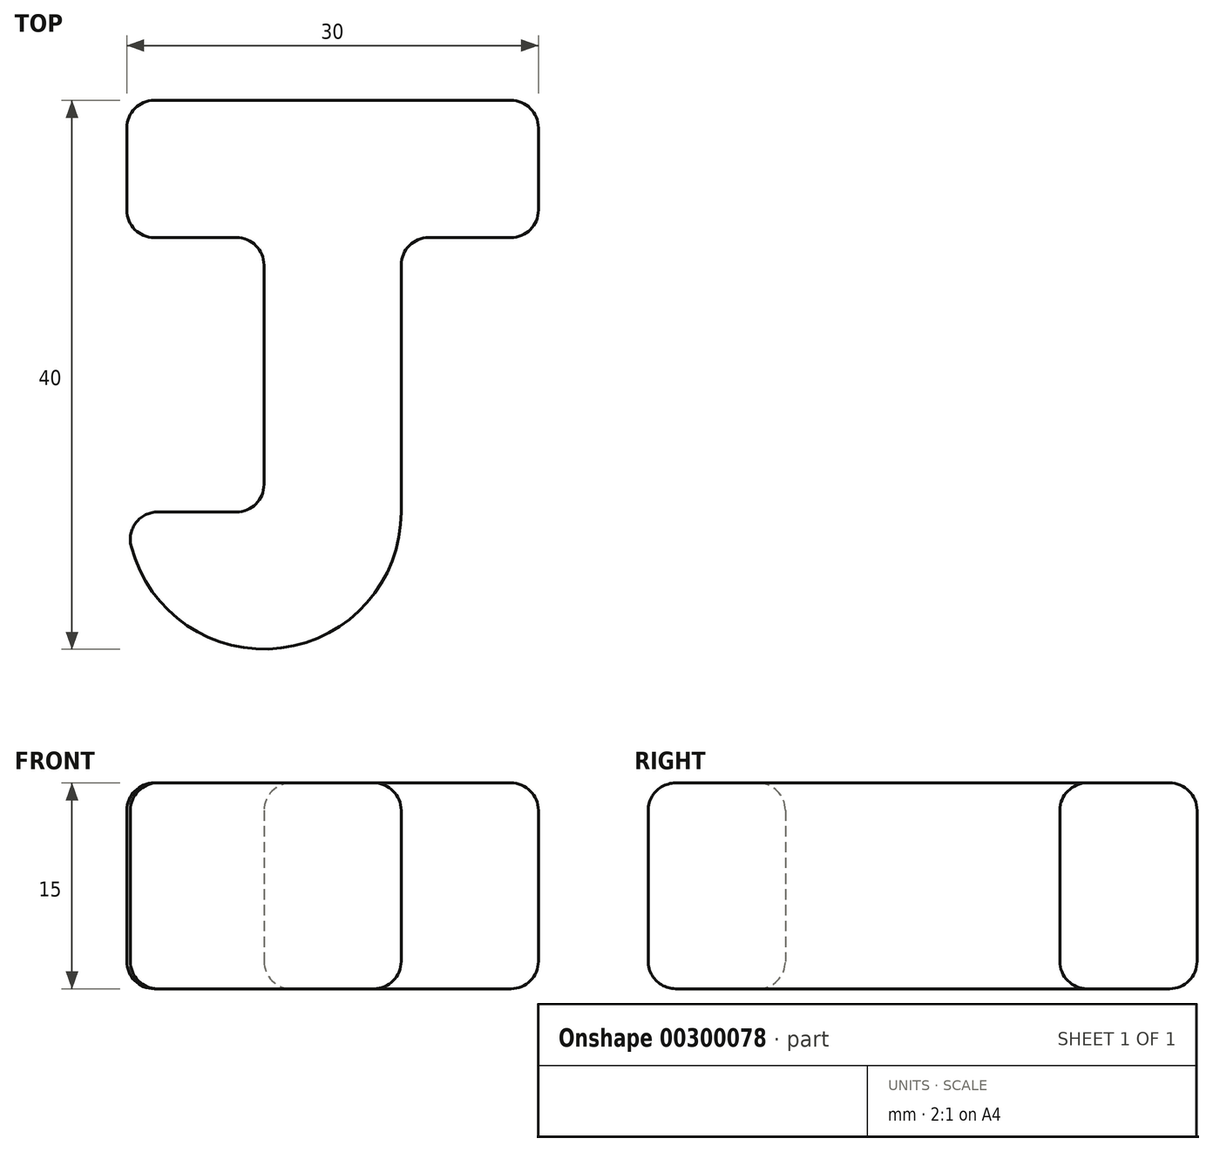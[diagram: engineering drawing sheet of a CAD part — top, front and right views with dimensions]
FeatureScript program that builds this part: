
annotation { "Feature Type Name" : "Feature", "Feature Type Description" : "" }
export const myFeature = defineFeature(function(context is Context, id is Id, definition is map)
    precondition{}
    {
        {
            var Q0;
            Q0=qCreatedBy(makeId("Top.planeOp"),FACE);
            var sketch = newSketch(context, id + "F0", { "sketchPlane" : qUnion([Q0])});
            skLineSegment(sketch, "E0", {"start": v(-30, 49.47) * mm, "end": v(0, 49.47) * mm});
            skLineSegment(sketch, "E1", {"start": v(0, 49.47) * mm, "end": v(0, 39.47) * mm});
            skLineSegment(sketch, "E2", {"start": v(0, 39.47) * mm, "end": v(-10, 39.47) * mm});
            skLineSegment(sketch, "E3", {"start": v(-10, 39.47) * mm, "end": v(-10, 19.47) * mm});
            skLineSegment(sketch, "E4", {"start": v(-30, 49.47) * mm, "end": v(-30, 39.47) * mm});
            skLineSegment(sketch, "E5", {"start": v(-30, 39.47) * mm, "end": v(-20, 39.47) * mm});
            skLineSegment(sketch, "E6", {"start": v(-20, 39.47) * mm, "end": v(-20, 19.47) * mm});
            skLineSegment(sketch, "E7", {"start": v(-20, 19.47) * mm, "end": v(-30, 19.47) * mm});
            skArc(sketch, "E8", {"start": v(-30, 19.47) * mm, "mid": v(-20, 9.47) * mm, "end": v(-10, 19.47) * mm});
            skSolve(sketch);
        }
        {
            var Q0;
            Q0=makeQuery(id+"F0.imprint","IMPRINT",FACE,{"disambiguationData":[TD([[makeQuery(id+"F0.imprint","IMPRINT",EDGE,{"derivedFrom":sQuery(id+"F0.wireOp",EDGE,"E0")}),-1.0]])]});
            extrude(context, id + "F1", {"entities" : qUnion([Q0]), "depth" : 15 * mm});
        }
        {
            var Q0;
            Q0=makeQuery(id+"F1.opExtrude","CAP_EDGE",EDGE,{"disambiguationData":[OSD([sQuery(id+"F0.wireOp",EDGE,"E5")])],"isStart":false});
            var Q1;
            Q1=makeQuery(id+"F1.opExtrude","CAP_EDGE",EDGE,{"disambiguationData":[OSD([sQuery(id+"F0.wireOp",EDGE,"E4")])],"isStart":false});
            var Q2;
            Q2=makeQuery(id+"F1.opExtrude","CAP_EDGE",EDGE,{"disambiguationData":[OSD([sQuery(id+"F0.wireOp",EDGE,"E0")])],"isStart":false});
            var Q3;
            Q3=makeQuery(id+"F1.opExtrude","CAP_EDGE",EDGE,{"disambiguationData":[OSD([sQuery(id+"F0.wireOp",EDGE,"E1")])],"isStart":false});
            var Q4;
            Q4=makeQuery(id+"F1.opExtrude","CAP_EDGE",EDGE,{"disambiguationData":[OSD([sQuery(id+"F0.wireOp",EDGE,"E2")])],"isStart":false});
            var Q5;
            Q5=makeQuery(id+"F1.opExtrude","CAP_EDGE",EDGE,{"disambiguationData":[OSD([sQuery(id+"F0.wireOp",EDGE,"E3")])],"isStart":false});
            var Q6;
            Q6=makeQuery(id+"F1.opExtrude","CAP_EDGE",EDGE,{"disambiguationData":[OSD([sQuery(id+"F0.wireOp",EDGE,"E8")])],"isStart":false});
            var Q7;
            Q7=makeQuery(id+"F1.opExtrude","CAP_EDGE",EDGE,{"disambiguationData":[OSD([sQuery(id+"F0.wireOp",EDGE,"E7")])],"isStart":false});
            var Q8;
            Q8=makeQuery(id+"F1.opExtrude","CAP_EDGE",EDGE,{"disambiguationData":[OSD([sQuery(id+"F0.wireOp",EDGE,"E6")])],"isStart":false});
            var Q9;
            Q9=makeQuery(id+"F1.opExtrude","SWEPT_EDGE",EDGE,{"disambiguationData":[OSD([sQuery(id+"F0.wireOp",EDGE,"E2"),sQuery(id+"F0.wireOp",EDGE,"E3")])]});
            var Q10;
            Q10=makeQuery(id+"F1.opExtrude","SWEPT_EDGE",EDGE,{"disambiguationData":[OSD([sQuery(id+"F0.wireOp",EDGE,"E1"),sQuery(id+"F0.wireOp",EDGE,"E2")])]});
            var Q11;
            Q11=makeQuery(id+"F1.opExtrude","SWEPT_EDGE",EDGE,{"disambiguationData":[OSD([sQuery(id+"F0.wireOp",EDGE,"E0"),sQuery(id+"F0.wireOp",EDGE,"E1")])]});
            var Q12;
            Q12=makeQuery(id+"F1.opExtrude","SWEPT_EDGE",EDGE,{"disambiguationData":[OSD([sQuery(id+"F0.wireOp",EDGE,"E4"),sQuery(id+"F0.wireOp",EDGE,"E5")])]});
            var Q13;
            Q13=makeQuery(id+"F1.opExtrude","SWEPT_EDGE",EDGE,{"disambiguationData":[OSD([sQuery(id+"F0.wireOp",EDGE,"E0"),sQuery(id+"F0.wireOp",EDGE,"E4")])]});
            var Q14;
            Q14=makeQuery(id+"F1.opExtrude","SWEPT_EDGE",EDGE,{"disambiguationData":[OSD([sQuery(id+"F0.wireOp",EDGE,"E7"),sQuery(id+"F0.wireOp",EDGE,"E8")])]});
            var Q15;
            Q15=makeQuery(id+"F1.opExtrude","SWEPT_EDGE",EDGE,{"disambiguationData":[OSD([sQuery(id+"F0.wireOp",EDGE,"E6"),sQuery(id+"F0.wireOp",EDGE,"E7")])]});
            var Q16;
            Q16=makeQuery(id+"F1.opExtrude","CAP_EDGE",EDGE,{"disambiguationData":[OSD([sQuery(id+"F0.wireOp",EDGE,"E7")])],"isStart":true});
            var Q17;
            Q17=makeQuery(id+"F1.opExtrude","CAP_EDGE",EDGE,{"disambiguationData":[OSD([sQuery(id+"F0.wireOp",EDGE,"E5")])],"isStart":true});
            var Q18;
            Q18=makeQuery(id+"F1.opExtrude","CAP_EDGE",EDGE,{"disambiguationData":[OSD([sQuery(id+"F0.wireOp",EDGE,"E0")])],"isStart":true});
            var Q19;
            Q19=makeQuery(id+"F1.opExtrude","CAP_EDGE",EDGE,{"disambiguationData":[OSD([sQuery(id+"F0.wireOp",EDGE,"E4")])],"isStart":true});
            var Q20;
            Q20=makeQuery(id+"F1.opExtrude","CAP_EDGE",EDGE,{"disambiguationData":[OSD([sQuery(id+"F0.wireOp",EDGE,"E8")])],"isStart":true});
            var Q21;
            Q21=makeQuery(id+"F1.opExtrude","CAP_FACE",FACE,{"disambiguationData":[OSD([sQuery(id+"F0.wireOp",EDGE,"E0"),sQuery(id+"F0.wireOp",EDGE,"E1"),sQuery(id+"F0.wireOp",EDGE,"E2"),sQuery(id+"F0.wireOp",EDGE,"E3"),sQuery(id+"F0.wireOp",EDGE,"E4"),sQuery(id+"F0.wireOp",EDGE,"E5"),sQuery(id+"F0.wireOp",EDGE,"E6"),sQuery(id+"F0.wireOp",EDGE,"E7"),sQuery(id+"F0.wireOp",EDGE,"E8")])],"isStart":true});
            var Q22;
            Q22=makeQuery(id+"F1.opExtrude","SWEPT_EDGE",EDGE,{"disambiguationData":[OSD([sQuery(id+"F0.wireOp",EDGE,"E5"),sQuery(id+"F0.wireOp",EDGE,"E6")])]});
            fillet(context, id + "F2", {"entities" : qUnion([Q0, Q1, Q2, Q3, Q4, Q5, Q6, Q7, Q8, Q9, Q10, Q11, Q12, Q13, Q14, Q15, Q16, Q17, Q18, Q19, Q20, Q21, Q22]), "radius" : 2 * mm, "tangentPropagation" : true, "allowEdgeOverflow" : false});
        }
    });
